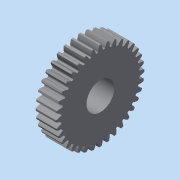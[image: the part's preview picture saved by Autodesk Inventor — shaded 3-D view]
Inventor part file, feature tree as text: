
AUTODESK INVENTOR PART (.ipt)
format: ipt  version: 2015 (Build 190159000, 159)  size: 1,423,872 bytes
history: native  units: in
note: dims shown in document units (in); Inventor stores cm internally (conversion verified against a paired STEP export)
features: other x1, plane x1, split x1, imported_body x1
ambient origin geometry x8: Origin, YZ Plane, XZ Plane, XY Plane, X Axis, Y Axis, Z Axis, Center Point
bodies: Solid1 (feature_tree)
feature tree (4):
  other  "s1086z-048s0361"
  plane  "Work Plane1"
  split  "Split1"
  imported_body  "Base1"
